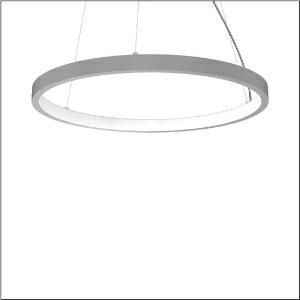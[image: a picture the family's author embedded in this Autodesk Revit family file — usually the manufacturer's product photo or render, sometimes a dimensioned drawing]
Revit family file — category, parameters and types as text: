
# Revit family: silica_r__21_ring-i_5pjbi4d1204a_fa15
name_source: partatom
category: Lighting Fixtures
units: mm (PartAtom-declared; Revit-internal decimal feet)

## family parameters
Cut with Voids When Loaded = No
Host = Face
Light Source = No
Part Type = Normal
Room Calculation Point = No
Round Connector Dimension = Use Diameter
Shared = No

## types (1)
- Silica® 21 Ring-I (1 x LED, 8460 lm, 140 W, 3000K)
    Apparent Load = 140 VA
    CIE Flux Codes = 22 48 76 50 101
    Color Rendering = 80
    Color Temperature = 3000K
    Default Elevation = 1800 mm
    Description = Silica® 21 Ring-I, suspended luminaire, of PMMA, frosted, light emission: inner ring side luminous distribution, primary light characteristic: symmetric, installation type: suspended mounting, LED, rated luminous flux: 8.460lm, luminous efficacy: 61lm/W, light colour: 830, colour temperature: 3000K, with terminal, 5-pole, mains connection: 230V, AC/DC, 0/50..60Hz, rated input power: 140W, housing, of extruded aluminium section, metallic grey (RAL 9006), diameter: 1.470mm, ceiling canopy, metallic grey (RAL 9006), protection rating (lamp compartment): IP40, insulation class (complete): insulation class I (protective earthing), certification: CE, impact resistance: IK02, permissible operating ambient temperature: 0..+35°C, packaging unit: 1 piece
    Height = 48 mm  [stored 0.15748 ft]
    Lamp = 1 x LED
    Lamp Light Flux = 8460 lm
    Lamp Power = 140 W
    Lamp count = 1
    Length = 1470 mm
    Luminous efficacy = 60 lm/W
    Manufacturer = Siteco
    ModVariant = No
    Model = 5PJBI4D1204A
    Mounting Place = Ceiling
    Mounting Type = Pendant
    Number of Poles = 1
    OnlyDefault = Yes
    Power Factor = 1
    Product Name = Silica® 21 Ring-I
    Product group = suspended luminaire
    ProductGroupID = 904
    Protection Class = Protection class I
    Protection Degree = IP 40
    RLX_Detail_Level = 1
    RLX_Emergency_Light_Flux = 0 lm
    RLX_Emergency_Type = 0
    RLX_Emergency_Type_DB = No
    RlxData = <blob elided: 18829 chars, md5=63bcbf5d>
    Socket = socket
    Standby Power = 0 W
    System Light Flux = 8460 lm
    System Power = 140 W
    Type Comments = Product without accessories
    Type Image = l_1251756.jpg
    URL = http://relux.com
    VarID = ---
    Voltage = 0 V
    Weight = 0.00 kg
    Width = 0 mm  [stored 0 ft]

note: [stored X ft] marks values corroborated as IEEE doubles in the binary element streams (Revit-internal decimal feet)

## geometry (parser evidence)
native form markers: Blend x4, Sweep x16
no freeform markers — native parametric forms only
